# Revit family: Shower-Shower_Trim-KOHLER-Singulier-K-TS10447
name_source: partatom
category: Plumbing Fixtures
revit_build: Autodesk Revit 2015 (Build: 20140606_1530(x64)
units: mm (PartAtom-declared; Revit-internal decimal feet)

## types (1)
- CP-Polished Chrome
    ADA Compliant = No
    Assembly Code = D2010700
    CW Connection = No
    Cold Water Inlet = Cold Water Inlet
    Date Modified = 05/30/2019
    Default Elevation = 42"
    Description = Shower valve trim includes a 2.5 gpm showerhead and a metal lever handle. Pair this trim with a Rite-Temp pressure-balancing valve
    Drain Included = No
    Finish = Kohler-Metal-CP-Polished_Chrome
    Flow Rate = 3 GPM
    HW Connection = Yes
    Height = 7 3/16"
    Length = 9 1/4"
    Manufacturer = KOHLER Co.
    MasterFormat 1995 = 15410
    MasterFormat 2004 = 22.41.23
    Material = Premium Metal Construction
    Model = K-TS10447-4-CP
    Pressure = 80.00 psi
    Product Documentation Link = https://www.us.kohler.com
    Product Name = Singulier
    Product Page URL = http://www.us.kohler.com
    Tempered Water Inlet = Tempered Water Inlet
    URL = https://www.us.kohler.com
    Vent Connection = No
    Waste Connection = No
    Waste Water Outlet = Waste Water Outlet
    WaterSense Certified = No
    Width = 6 3/8"

## geometry (parser evidence)
native form markers: Sweep x9
no freeform markers — native parametric forms only
